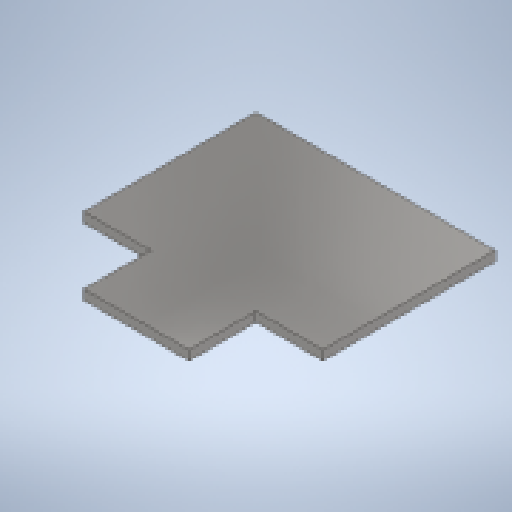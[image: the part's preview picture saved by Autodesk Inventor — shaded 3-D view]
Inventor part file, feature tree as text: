
AUTODESK INVENTOR PART (.ipt)
format: ipt  version: 2023 (Build 270158000, 158)  size: 163,328 bytes
history: native  units: mm
features: other x4, extrude x3, sketch x3, projected_geometry x2, reference x1
ambient origin geometry x8: Origin, YZ Plane, XZ Plane, XY Plane, X Axis, Y Axis, Z Axis, Center Point
bodies: Body1 (feature_tree)
feature tree (13):
  other  "Bryła1"
  extrude  "Wyciągnięcie proste1"  Depth=50.0mm
  extrude  "Wyciągnięcie proste2"  Depth=50.0mm
  extrude  "Wyciągnięcie proste4"  Depth=2.0mm TaperAngle=0.0deg
  sketch  "Szkic1"
  sketch  "Szkic2"
  projected_geometry  "Pętla rzutowana1"
  sketch  "Szkic4"
  projected_geometry  "Pętla rzutowana3"
  reference  "Odniesienie2"
  other  "<userpath>\Documents\Inventor\MikroNalesnik\byk.iam"
  other  "byk.iam"
  other  "noz:1"
